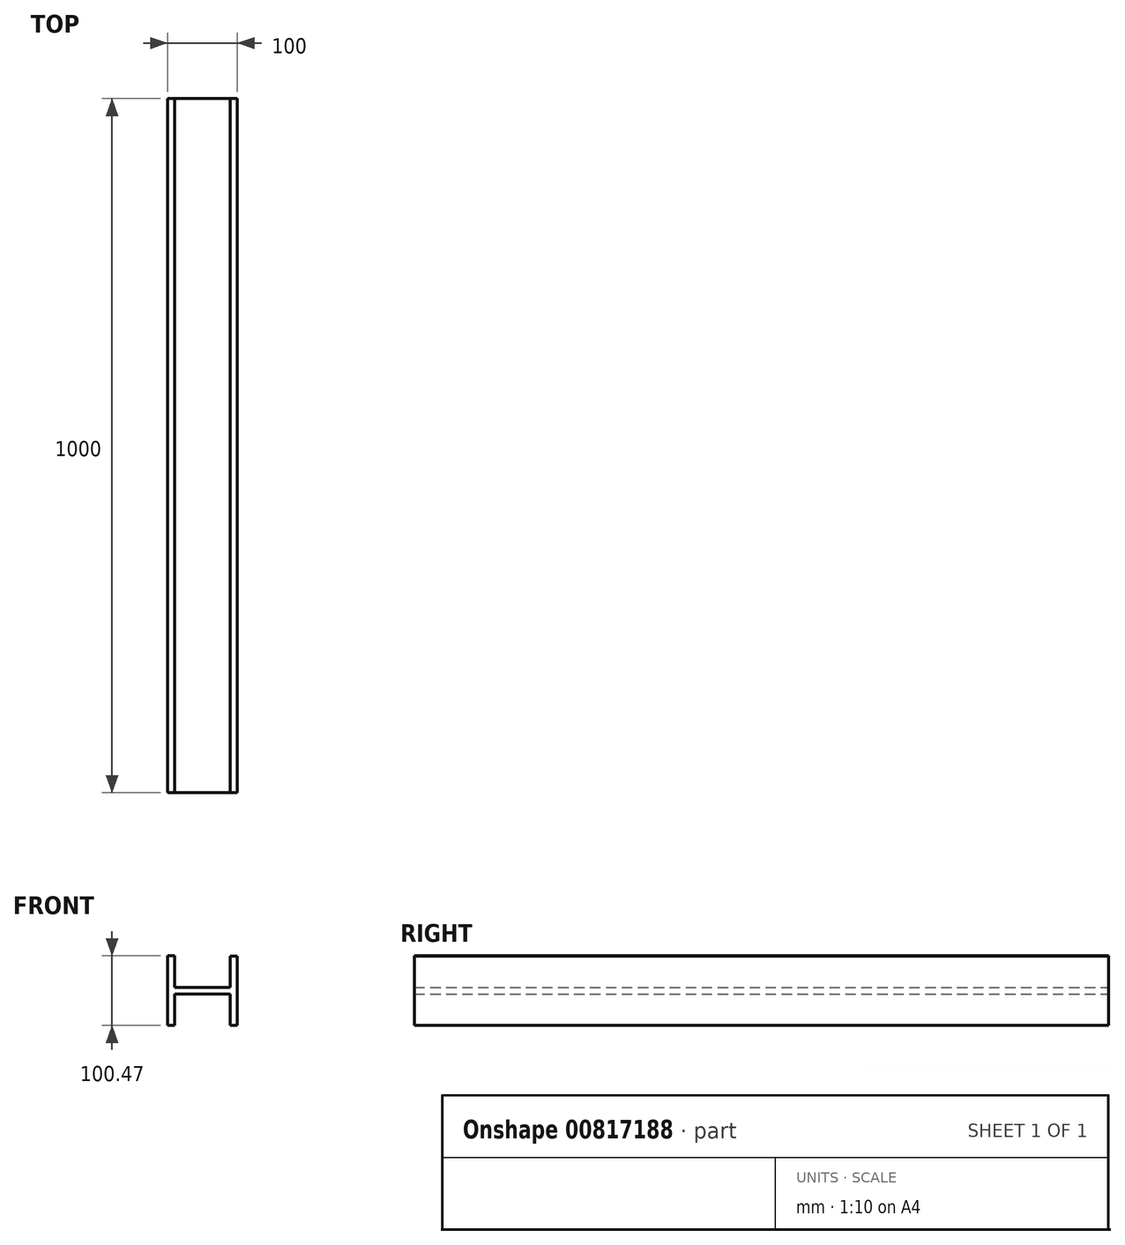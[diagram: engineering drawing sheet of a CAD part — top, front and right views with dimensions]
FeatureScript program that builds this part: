
annotation { "Feature Type Name" : "Feature", "Feature Type Description" : "" }
export const myFeature = defineFeature(function(context is Context, id is Id, definition is map)
    precondition{}
    {
        {
            var Q0;
            Q0=qCreatedBy(makeId("Front.planeOp"),FACE);
            var sketch = newSketch(context, id + "F0", { "sketchPlane" : qUnion([Q0])});
            skLineSegment(sketch, "E0", {"start": v(0, 0) * mm, "end": v(-50, 0) * mm});
            skLineSegment(sketch, "E1.MirrorCS", {"start": v(0, 0) * mm, "end": v(50, 0) * mm});
            skLineSegment(sketch, "E2", {"start": v(-50, 0) * mm, "end": v(-50, -49.7) * mm});
            skLineSegment(sketch, "E3", {"start": v(-50, -49.7) * mm, "end": v(-50, 50.3) * mm});
            skLineSegment(sketch, "E4", {"start": v(50, 0) * mm, "end": v(50, -50.16) * mm});
            skLineSegment(sketch, "E5", {"start": v(50, -50.16) * mm, "end": v(50, 49.84) * mm});
            skLineSegment(sketch, "E6.0", {"start": v(-40, -49.7) * mm, "end": v(-40, 50.3) * mm});
            skLineSegment(sketch, "E7.0", {"start": v(40, -50.16) * mm, "end": v(40, 49.84) * mm});
            skLineSegment(sketch, "E8", {"start": v(-50, 50.3) * mm, "end": v(-40, 50.3) * mm});
            skLineSegment(sketch, "E9", {"start": v(40, 49.84) * mm, "end": v(50, 49.84) * mm});
            skLineSegment(sketch, "E10", {"start": v(40, -50.16) * mm, "end": v(50, -50.16) * mm});
            skLineSegment(sketch, "E11", {"start": v(-40, -49.7) * mm, "end": v(-50, -49.7) * mm});
            skLineSegment(sketch, "E12.0", {"start": v(0, 5) * mm, "end": v(-50, 5) * mm});
            skLineSegment(sketch, "E12.1", {"start": v(0, 5) * mm, "end": v(50, 5) * mm});
            skLineSegment(sketch, "E13.0", {"start": v(0, -5) * mm, "end": v(-50, -5) * mm});
            skLineSegment(sketch, "E13.1", {"start": v(0, -5) * mm, "end": v(50, -5) * mm});
            skSolve(sketch);
        }
        {
            var Q0;
            Q0 = qSketchRegion(id + "F0", true);
            extrude(context, id + "F1", {"entities" : qUnion([Q0]), "depth" : 1000 * mm, "offsetDistance" : 25 * mm});
        }
    });
